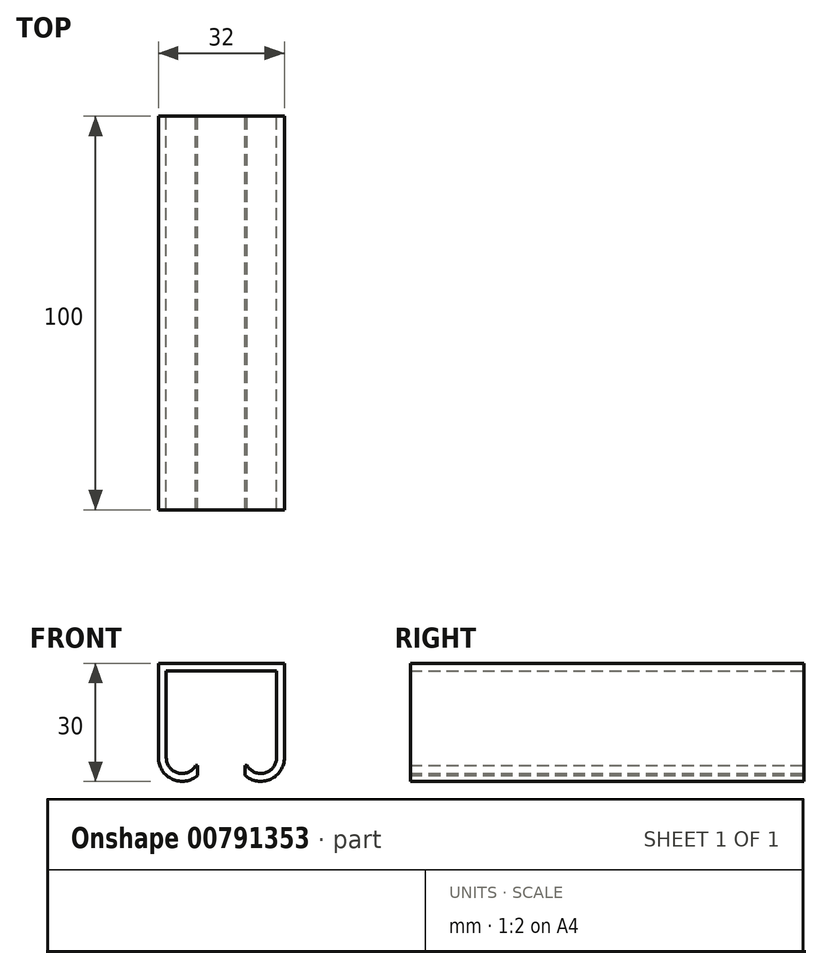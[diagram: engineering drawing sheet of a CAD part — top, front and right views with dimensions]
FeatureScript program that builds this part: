
annotation { "Feature Type Name" : "Feature", "Feature Type Description" : "" }
export const myFeature = defineFeature(function(context is Context, id is Id, definition is map)
    precondition{}
    {
        {
            var Q0;
            Q0=qCreatedBy(makeId("Front.planeOp"),FACE);
            var sketch = newSketch(context, id + "F0", { "sketchPlane" : qUnion([Q0])});
            skLineSegment(sketch, "E0", {"start": v(0, 0) * mm, "end": v(0, 30) * mm, "construction": true});
            skLineSegment(sketch, "E1", {"start": v(-16, 30) * mm, "end": v(16, 30) * mm});
            skArc(sketch, "E2", {"start": v(-16, 6) * mm, "mid": v(-12.45, 0.52) * mm, "end": v(-6, 1.53) * mm});
            skLineSegment(sketch, "E3", {"start": v(0, 0) * mm, "end": v(-22.17, 0) * mm, "construction": true});
            skLineSegment(sketch, "E4", {"start": v(-16, 30) * mm, "end": v(-16, 6) * mm});
            skLineSegment(sketch, "E5", {"start": v(-6, 0) * mm, "end": v(-6, 15.87) * mm, "construction": true});
            skArc(sketch, "E6.MirrorCS", {"start": v(16, 6) * mm, "mid": v(12.45, 0.52) * mm, "end": v(6, 1.53) * mm});
            skLineSegment(sketch, "E7.MirrorCS", {"start": v(16, 30) * mm, "end": v(16, 6) * mm});
            skArc(sketch, "E8.0", {"start": v(-14, 6) * mm, "mid": v(-11.04, 2.14) * mm, "end": v(-6.54, 4) * mm});
            skLineSegment(sketch, "E8.2", {"start": v(14, 28) * mm, "end": v(14, 6) * mm});
            skLineSegment(sketch, "E8.3", {"start": v(-14, 28) * mm, "end": v(14, 28) * mm});
            skLineSegment(sketch, "E8.4", {"start": v(-14, 28) * mm, "end": v(-14, 6) * mm});
            skLineSegment(sketch, "E9", {"start": v(-6, 4) * mm, "end": v(-6, 1.53) * mm});
            skArc(sketch, "E10.MirrorCS", {"start": v(14, 6) * mm, "mid": v(11.04, 2.14) * mm, "end": v(6.54, 4) * mm});
            skLineSegment(sketch, "E11.MirrorCS", {"start": v(6, 4) * mm, "end": v(6, 1.53) * mm});
            skLineSegment(sketch, "E12", {"start": v(-6.54, 4) * mm, "end": v(6.54, 4) * mm, "construction": true});
            skPoint(sketch, "E13.orphan", {"position": v(-6, 6) * mm});
            skPoint(sketch, "E14.orphan", {"position": v(6, 6) * mm});
            skLineSegment(sketch, "E15", {"start": v(-6.54, 4) * mm, "end": v(-6, 4) * mm});
            skLineSegment(sketch, "E16", {"start": v(6.54, 4) * mm, "end": v(6, 4) * mm});
            skSolve(sketch);
        }
        {
            var Q0;
            Q0=makeQuery(id+"F0.imprint","IMPRINT",FACE,{"disambiguationData":[TD([[makeQuery(id+"F0.imprint","IMPRINT",EDGE,{"derivedFrom":sQuery(id+"F0.wireOp",EDGE,"E1")}),-1.0]])]});
            extrude(context, id + "F1", {"entities" : qUnion([Q0]), "depth" : 100 * mm, "offsetDistance" : 25 * mm, "symmetric" : true});
        }
    });
